# Revit family: Shower-Shower_Column_Kit-KOHLER-Aleo-K-26243T_1
name_source: partatom
category: Plumbing Fixtures
units: mm (PartAtom-declared; Revit-internal decimal feet)

## family parameters
Cut with Voids When Loaded = No
Host = Face
Maintain Annotation Orientation = No
OmniClass Number = 23.31.17.00
OmniClass Title = Showers
Part Type = Normal
Room Calculation Point = No
Round Connector Dimension = Use Diameter
Shared = No

## types (2) — shared parameters
ADA Compliant = No
Assembly Code = D2010700
CW Connection = Yes
Cold Water Inlet = Cold Water Inlet
Date Modified = 04/22/2022
Default Elevation = 36"
Description = Leo thermostatic three-outlet shower column hard pipe connection (rectangular head)
Drain Included = No
Flow Rate = 0 GPM
HW Connection = Yes
Height = 48 3/4"
Hot Water Inlet = Hot Water Inlet
Length = 23 5/8"
Manufacturer = Kohler Co.
Master Format 2014 = 22 42 23
Master Format 2014 Name = Residential Showers
Material = Premium Metal Construction
Pressure = 0.00 psi
Product Documentation Link = https://files.kohler.com.cn
Product Name = Aleo
Product Page URL = https://www.kohler.com.cn
Spout Reach = 4 1/2"
URL = http://www.kohler.com.cn
Vent Connection = No
Waste Connection = No
Waste Water Outlet = Waste Water Outlet
WaterSense Certified = No
Width = 5 7/8"

## per-type parameters (varying)
| type | Finish | Model | Type |
| CP-Polished Chrome | Kohler-Metal-CP-Polished_Chrome | K-26243T-9-CP | 1 |
| BL-Matte Black | Kohler-Metal-BL-Matte_Black | K-26243T-9-BL | 2 |

## geometry (parser evidence)
native form markers: Sweep x4
no freeform markers — native parametric forms only
